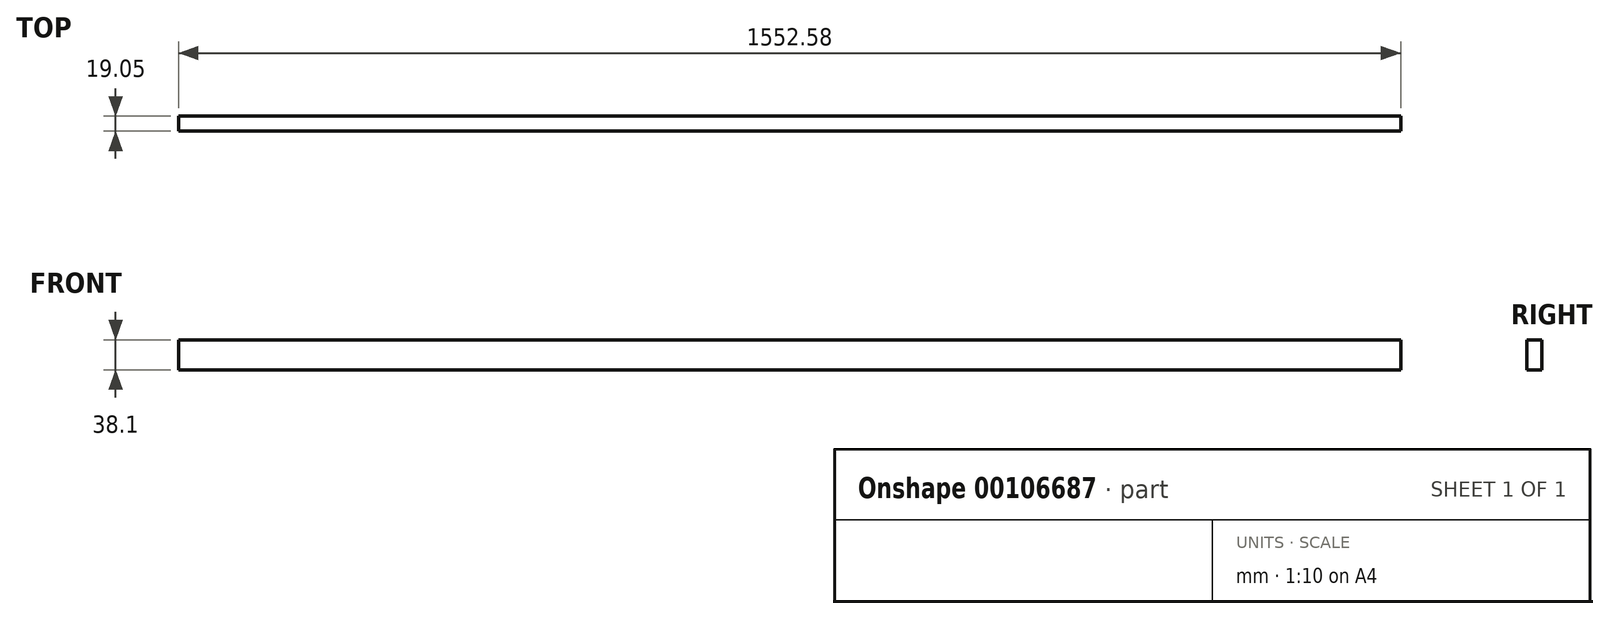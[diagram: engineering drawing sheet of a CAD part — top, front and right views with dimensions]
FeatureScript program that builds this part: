
annotation { "Feature Type Name" : "Feature", "Feature Type Description" : "" }
export const myFeature = defineFeature(function(context is Context, id is Id, definition is map)
    precondition{}
    {
        {
            var Q0;
            Q0=qCreatedBy(makeId("Front.planeOp"),FACE);
            var sketch = newSketch(context, id + "F0", { "sketchPlane" : qUnion([Q0])});
            skLineSegment(sketch, "E0.bottom", {"start": v(0, 0) * mm, "end": v(1552.58, 0) * mm});
            skLineSegment(sketch, "E0.top", {"start": v(0, 38.1) * mm, "end": v(1552.58, 38.1) * mm});
            skLineSegment(sketch, "E0.left", {"start": v(0, 0) * mm, "end": v(0, 38.1) * mm});
            skLineSegment(sketch, "E0.right", {"start": v(1552.58, 0) * mm, "end": v(1552.58, 38.1) * mm});
            skSolve(sketch);
        }
        {
            var Q0;
            Q0=makeQuery(id+"F0.imprint","IMPRINT",FACE,{"disambiguationData":[TD([[makeQuery(id+"F0.imprint","IMPRINT",EDGE,{"derivedFrom":sQuery(id+"F0.wireOp",EDGE,"E0.bottom")}),1.0]])]});
            extrude(context, id + "F1", {"entities" : qUnion([Q0]), "depth" : 19.05 * mm});
        }
    });
